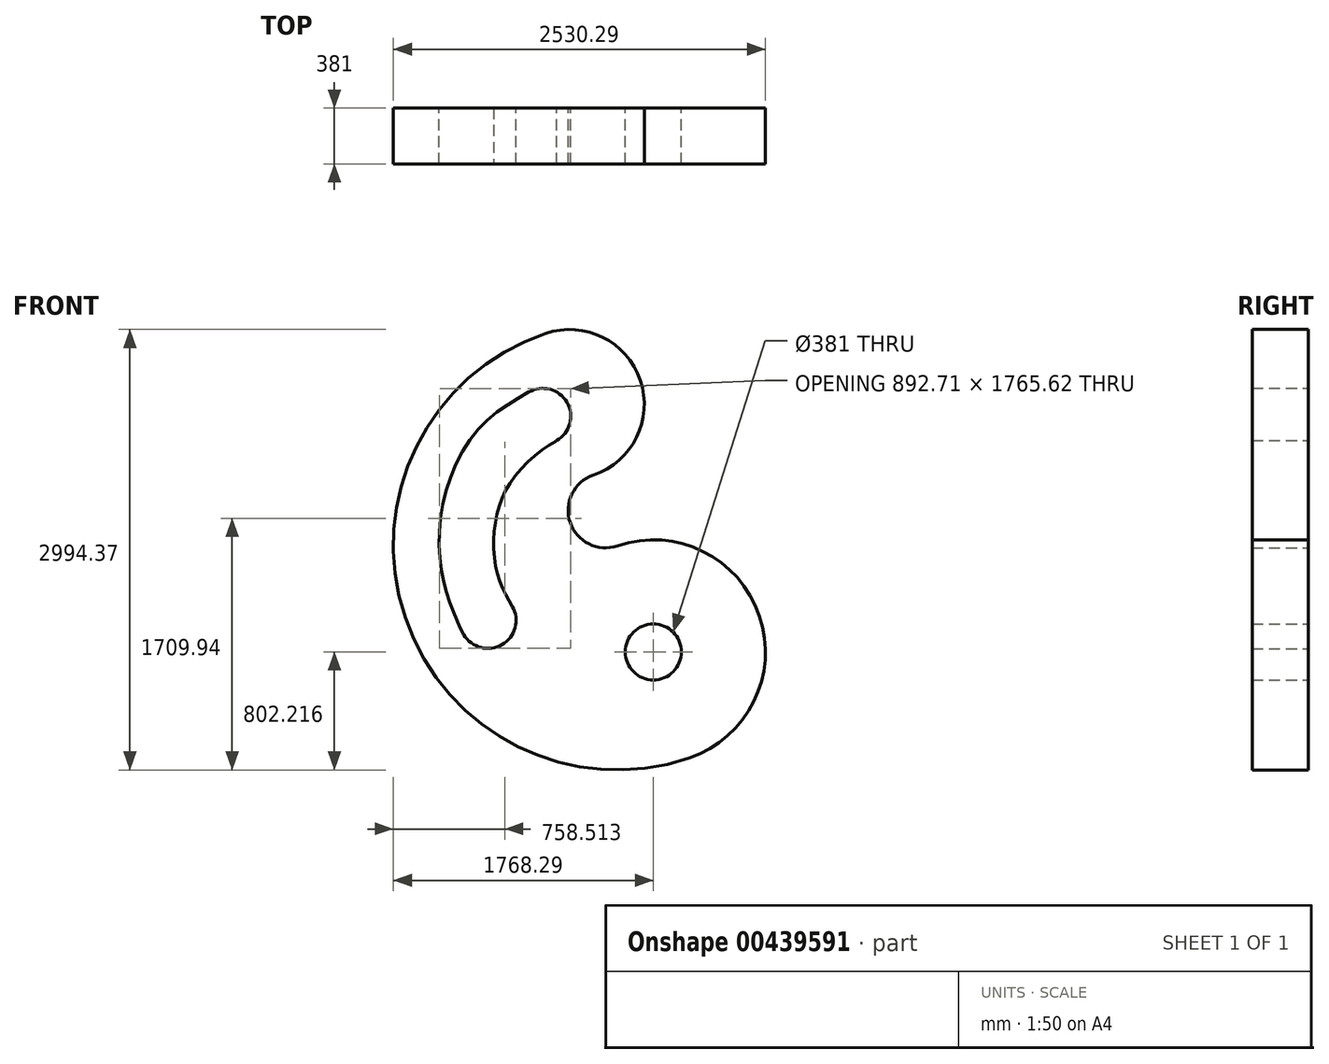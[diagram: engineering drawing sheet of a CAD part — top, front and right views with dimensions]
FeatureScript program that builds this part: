
annotation { "Feature Type Name" : "Feature", "Feature Type Description" : "" }
export const myFeature = defineFeature(function(context is Context, id is Id, definition is map)
    precondition{}
    {
        {
            var Q0;
            Q0=qCreatedBy(makeId("Front.planeOp"),FACE);
            var sketch = newSketch(context, id + "F0", { "sketchPlane" : qUnion([Q0])});
            skArc(sketch, "E0", {"start": v(162.86, -481.19) * mm, "mid": v(481.19, 162.86) * mm, "end": v(-162.86, 481.19) * mm});
            skArc(sketch, "E1", {"start": v(162.86, -481.19) * mm, "mid": v(3.7, -803.21) * mm, "end": v(325.72, -962.37) * mm});
            skArc(sketch, "E2", {"start": v(814.3, -2405.93) * mm, "mid": v(1291.79, -1439.86) * mm, "end": v(325.72, -962.37) * mm});
            skArc(sketch, "E3", {"start": v(-162.86, 481.19) * mm, "mid": v(-1117.84, -1450.95) * mm, "end": v(814.3, -2405.93) * mm});
            skLineSegment(sketch, "E4", {"start": v(-86.88, -247.74) * mm, "end": v(-87.03, -247.47) * mm});
            skArc(sketch, "E5", {"start": v(-94.9, -251.77) * mm, "mid": v(-15.1, 8.84) * mm, "end": v(-277.53, 82.49) * mm});
            skArc(sketch, "E6", {"start": v(-719.14, -1565.62) * mm, "mid": v(-458.91, -1635.35) * mm, "end": v(-389.18, -1375.12) * mm});
            skPoint(sketch, "E7.4.internal.snap0", {"position": v(-614.7, -1505.33) * mm});
            skFitSpline(sketch, "E7", {"points": [v(-719.14, -1565.62) * mm, v(-796.98, -1393.17) * mm, v(-878.77, -1077.8) * mm, v(-844.8, -612.5) * mm, v(-614.7, -163.04) * mm, v(-277.53, 82.49) * mm], "startDerivative": vector(-612.18, 1060.33) * mm, "endDerivative": vector(1661.76, 959.42) * mm});
            skFitSpline(sketch, "E8", {"points": [v(-389.18, -1375.12) * mm, v(-491.35, -1149.46) * mm, v(-504.72, -803.06) * mm, v(-371.27, -490.24) * mm, v(-86.88, -247.74) * mm], "startDerivative": vector(-536.16, 928.65) * mm, "endDerivative": vector(967.85, 472.83) * mm});
            skPoint(sketch, "E9.trimOffspring.end.orphan", {"position": v(-499.47, 466.9) * mm});
            skArc(sketch, "E10.trimOffspring", {"start": v(0, 0) * mm, "mid": v(-4.55, -1.55) * mm, "end": v(-9.1, -3.13) * mm});
            skPoint(sketch, "E11.start.orphan", {"position": v(325.72, 534.28) * mm});
            skPoint(sketch, "E12.trimOffspring.end.orphan", {"position": v(-1555.13, -2048.28) * mm});
            skLineSegment(sketch, "E13.trimOffspring", {"start": v(-554.16, -1470.37) * mm, "end": v(-614.7, -1505.33) * mm});
            skCircle(sketch, "E14", {"center": v(570, -1684.15) * mm, "radius": 190.5 * mm});
            skSolve(sketch);
        }
        {
            var Q0;
            Q0=makeQuery(id+"F0.imprint","IMPRINT",FACE,{"disambiguationData":[TD([[makeQuery(id+"F0.imprint","IMPRINT",EDGE,{"derivedFrom":sQuery(id+"F0.wireOp",EDGE,"E0")}),1.0]])]});
            extrude(context, id + "F1", {"entities" : qUnion([Q0]), "depth" : 381 * mm});
        }
    });
